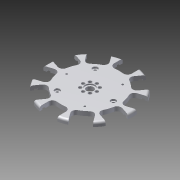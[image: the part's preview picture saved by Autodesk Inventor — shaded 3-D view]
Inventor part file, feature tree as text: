
AUTODESK INVENTOR PART (.ipt)
format: ipt  version: 2015 (Build 190159000, 159)  size: 379,904 bytes
history: native  units: in
note: dims shown in document units (in); Inventor stores cm internally (conversion verified against a paired STEP export)
features: fillet x1, other x1, imported_body x1
ambient origin geometry x8: Origin, YZ Plane, XZ Plane, XY Plane, X Axis, Y Axis, Z Axis, Center Point
bodies: Body1 (feature_tree)
feature tree (3):
  fillet  "Fillet2"  [1 undecoded]
  other  "tetrix_731132_hub1"
  imported_body  "Base1"
note: 1 required parameter value undecoded (feature->parameter linkage not recoverable at this tier; creation-order binding heuristic only, values carry confidence <= 0.55)
